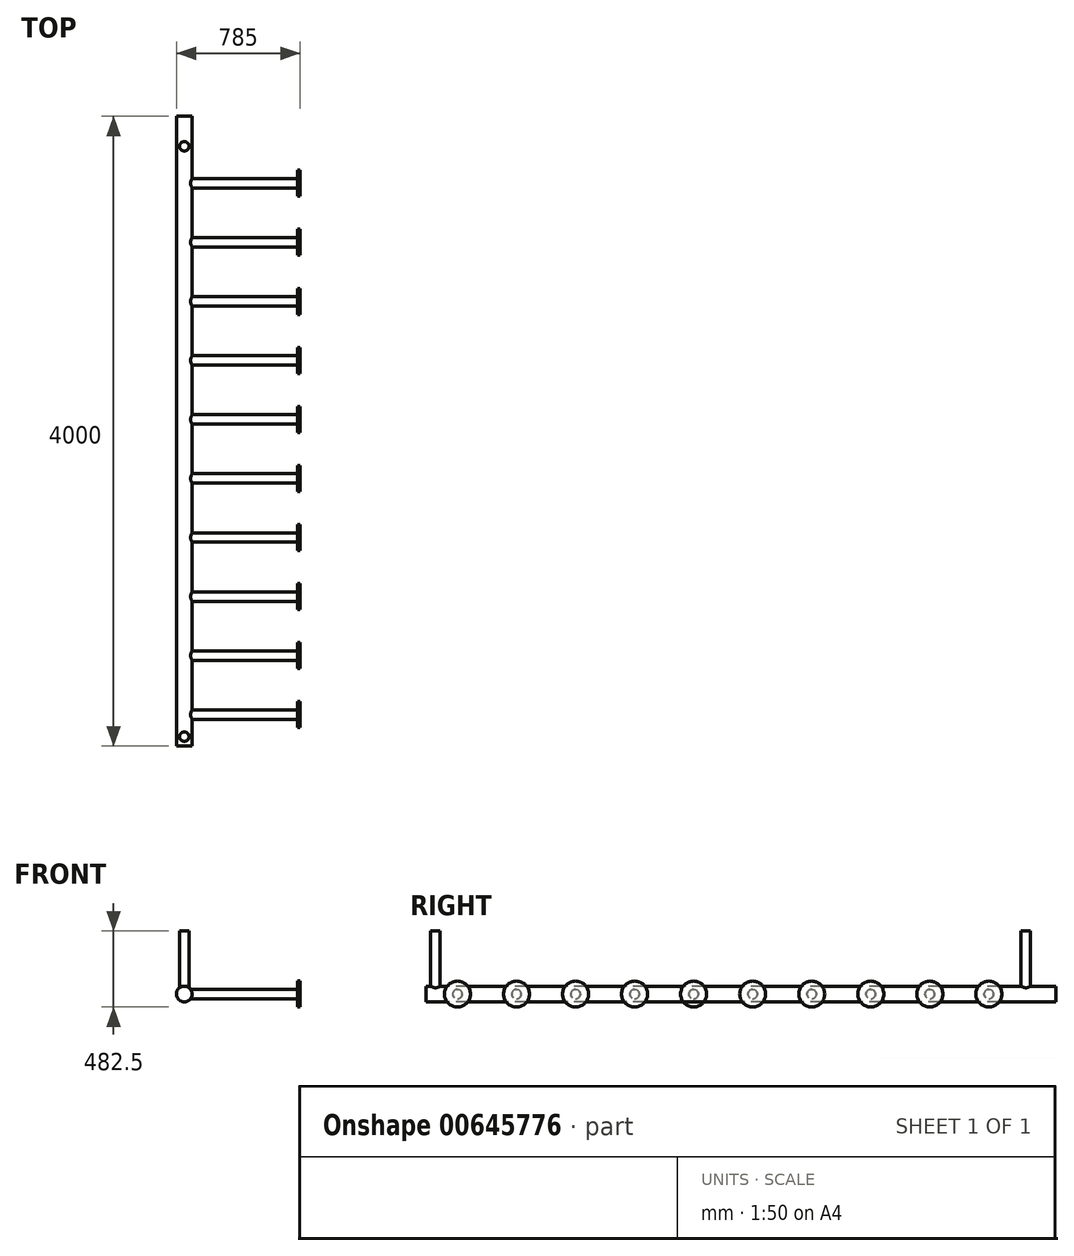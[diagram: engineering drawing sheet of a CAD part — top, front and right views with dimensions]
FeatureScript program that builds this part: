
annotation { "Feature Type Name" : "Feature", "Feature Type Description" : "" }
export const myFeature = defineFeature(function(context is Context, id is Id, definition is map)
    precondition{}
    {
        {
            var Q0;
            Q0=qCreatedBy(makeId("Front.planeOp"),FACE);
            var sketch = newSketch(context, id + "F0", { "sketchPlane" : qUnion([Q0])});
            skCircle(sketch, "E0", {"center": v(0, 0) * mm, "radius": 50 * mm});
            skSolve(sketch);
        }
        {
            var Q0;
            Q0=makeQuery(id+"F0.imprint","IMPRINT",FACE,{"disambiguationData":[TD([[makeQuery(id+"F0.imprint","IMPRINT",EDGE,{"derivedFrom":sQuery(id+"F0.wireOp",EDGE,"E0")}),1.0]])]});
            extrude(context, id + "F1", {"entities" : qUnion([Q0]), "oppositeDirection" : true, "depth" : 4000 * mm, "offsetDistance" : 25 * mm});
        }
        {
            var Q0;
            Q0=qCreatedBy(makeId("Top.planeOp"),FACE);
            var sketch = newSketch(context, id + "F2", { "sketchPlane" : qUnion([Q0])});
            skCircle(sketch, "E1", {"center": v(0, 60) * mm, "radius": 30 * mm});
            skCircle(sketch, "E2", {"center": v(0, 3810) * mm, "radius": 30 * mm});
            skSolve(sketch);
        }
        {
            var Q0;
            Q0=qSketchRegion(id+"F2",true);
            extrude(context, id + "F3", {"entities" : qUnion([Q0]), "operationType" : NewBodyOperationType.ADD, "depth" : 400 * mm, "offsetDistance" : 25 * mm});
        }
        {
            var Q0;
            Q0=qCreatedBy(makeId("Right.planeOp"),FACE);
            var sketch = newSketch(context, id + "F4", { "sketchPlane" : qUnion([Q0])});
            skCircle(sketch, "E3", {"center": v(200, 0) * mm, "radius": 30 * mm});
            skCircle(sketch, "E4.1.0.0", {"center": v(575, 0) * mm, "radius": 30 * mm});
            skCircle(sketch, "E4.2.0.0", {"center": v(950, 0) * mm, "radius": 30 * mm});
            skCircle(sketch, "E4.3.0.0", {"center": v(1325, 0) * mm, "radius": 30 * mm});
            skCircle(sketch, "E4.4.0.0", {"center": v(1700, 0) * mm, "radius": 30 * mm});
            skCircle(sketch, "E4.5.0.0", {"center": v(2075, 0) * mm, "radius": 30 * mm});
            skCircle(sketch, "E4.6.0.0", {"center": v(2450, 0) * mm, "radius": 30 * mm});
            skCircle(sketch, "E4.7.0.0", {"center": v(2825, 0) * mm, "radius": 30 * mm});
            skCircle(sketch, "E4.8.0.0", {"center": v(3200, 0) * mm, "radius": 30 * mm});
            skCircle(sketch, "E4.9.0.0", {"center": v(3575, 0) * mm, "radius": 30 * mm});
            skLineSegment(sketch, "E4.direction1", {"start": v(200, 0) * mm, "end": v(575, 0) * mm, "construction": true});
            skSolve(sketch);
        }
        {
            var Q0;
            Q0=qSketchRegion(id+"F4",true);
            extrude(context, id + "F5", {"entities" : qUnion([Q0]), "operationType" : NewBodyOperationType.ADD, "depth" : 720 * mm, "offsetDistance" : 25 * mm});
        }
        {
            var Q0;
            Q0=makeQuery(id+"F5.opExtrude","CAP_FACE",FACE,{"disambiguationData":[OSD([sQuery(id+"F4.wireOp",EDGE,"E3")])],"isStart":false});
            var sketch = newSketch(context, id + "F6", { "sketchPlane" : qUnion([Q0])});
            skCircle(sketch, "E5", {"center": v(200, 0) * mm, "radius": 82.5 * mm});
            skCircle(sketch, "E6.1.0.0", {"center": v(575, 0) * mm, "radius": 82.5 * mm});
            skCircle(sketch, "E6.2.0.0", {"center": v(950, 0) * mm, "radius": 82.5 * mm});
            skCircle(sketch, "E6.3.0.0", {"center": v(1325, 0) * mm, "radius": 82.5 * mm});
            skCircle(sketch, "E6.4.0.0", {"center": v(1700, 0) * mm, "radius": 82.5 * mm});
            skCircle(sketch, "E6.5.0.0", {"center": v(2075, 0) * mm, "radius": 82.5 * mm});
            skCircle(sketch, "E6.6.0.0", {"center": v(2450, 0) * mm, "radius": 82.5 * mm});
            skCircle(sketch, "E6.7.0.0", {"center": v(2825, 0) * mm, "radius": 82.5 * mm});
            skCircle(sketch, "E6.8.0.0", {"center": v(3200, 0) * mm, "radius": 82.5 * mm});
            skCircle(sketch, "E6.9.0.0", {"center": v(3575, 0) * mm, "radius": 82.5 * mm});
            skLineSegment(sketch, "E6.direction1", {"start": v(200, 0) * mm, "end": v(575, 0) * mm, "construction": true});
            skSolve(sketch);
        }
        {
            var Q0;
            Q0=qSketchRegion(id+"F6",true);
            extrude(context, id + "F7", {"entities" : qUnion([Q0]), "operationType" : NewBodyOperationType.ADD, "depth" : 15 * mm, "offsetDistance" : 25 * mm});
        }
    });
